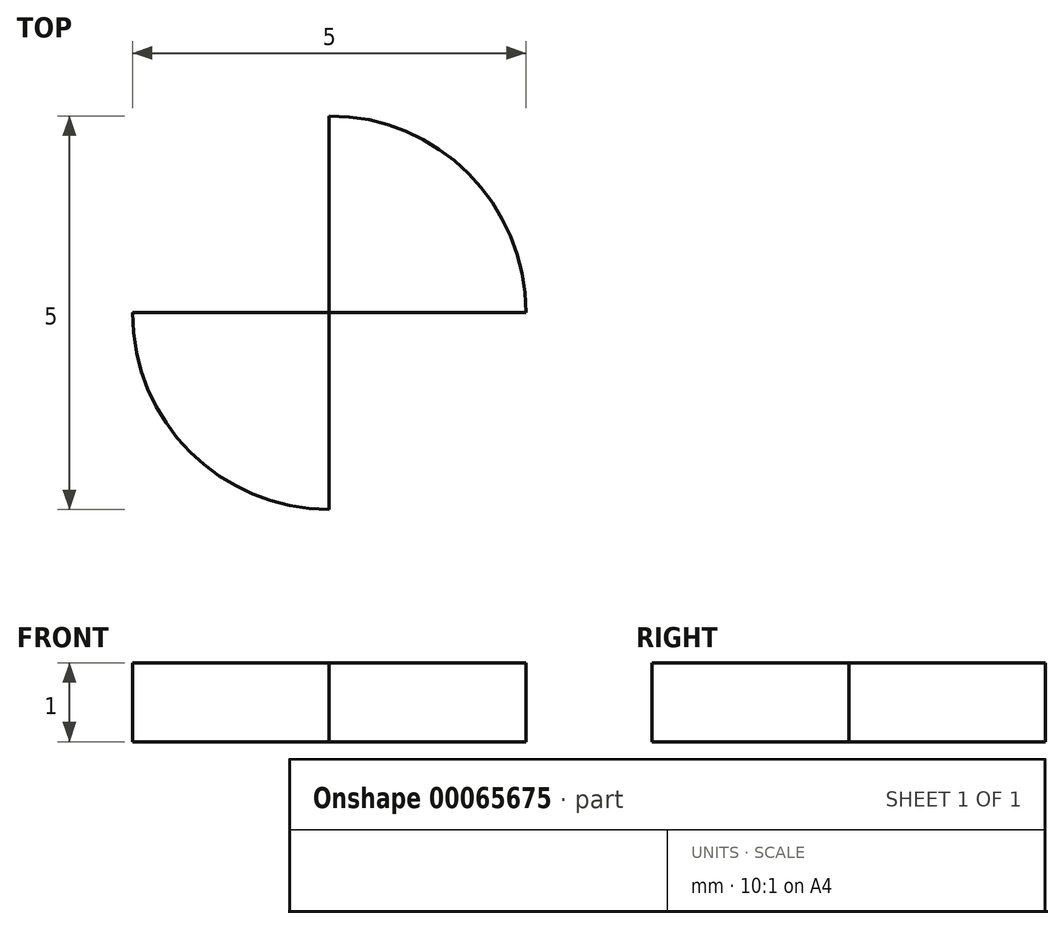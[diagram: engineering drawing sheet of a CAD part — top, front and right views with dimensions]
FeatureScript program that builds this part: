
annotation { "Feature Type Name" : "Feature", "Feature Type Description" : "" }
export const myFeature = defineFeature(function(context is Context, id is Id, definition is map)
    precondition{}
    {
        {
            var Q0;
            Q0=qCreatedBy(makeId("Top.planeOp"),FACE);
            var sketch = newSketch(context, id + "F0", { "sketchPlane" : qUnion([Q0])});
            skArc(sketch, "E0", {"start": v(-2.5, 0) * mm, "mid": v(-1.77, -1.77) * mm, "end": v(0, -2.5) * mm});
            skLineSegment(sketch, "E1", {"start": v(0, 0) * mm, "end": v(0, 2.5) * mm});
            skLineSegment(sketch, "E2", {"start": v(-2.5, 0) * mm, "end": v(0, 0) * mm});
            skLineSegment(sketch, "E3", {"start": v(0, 0) * mm, "end": v(0, -2.5) * mm});
            skLineSegment(sketch, "E4", {"start": v(0, -2.5) * mm, "end": v(0, 0) * mm});
            skLineSegment(sketch, "E5", {"start": v(2.5, 0) * mm, "end": v(0, 0) * mm});
            skArc(sketch, "E6.trimOffspring", {"start": v(2.5, 0) * mm, "mid": v(1.77, 1.77) * mm, "end": v(0, 2.5) * mm});
            skSolve(sketch);
        }
        {
            var Q0;
            Q0=makeQuery(id+"F0.imprint","IMPRINT",FACE,{"disambiguationData":[TD([[makeQuery(id+"F0.imprint","IMPRINT",EDGE,{"derivedFrom":sQuery(id+"F0.wireOp",EDGE,"E0")}),1.0]])]});
            var Q1;
            Q1=makeQuery(id+"F0.imprint","IMPRINT",FACE,{"disambiguationData":[TD([[makeQuery(id+"F0.imprint","IMPRINT",EDGE,{"derivedFrom":sQuery(id+"F0.wireOp",EDGE,"E1")}),-1.0]])]});
            extrude(context, id + "F1", {"entities" : qUnion([Q0, Q1]), "depth" : 1 * mm});
        }
    });
